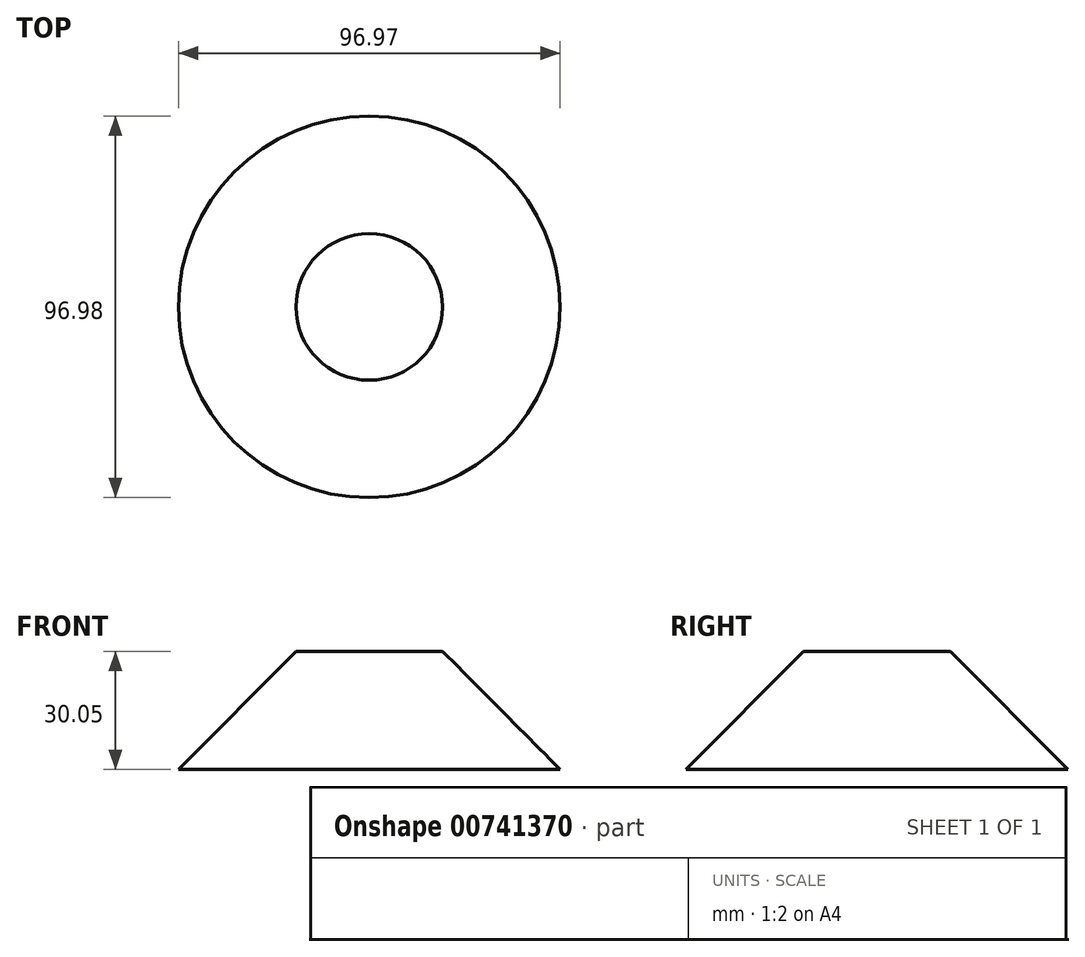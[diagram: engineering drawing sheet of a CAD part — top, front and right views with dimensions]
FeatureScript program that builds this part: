
annotation { "Feature Type Name" : "Feature", "Feature Type Description" : "" }
export const myFeature = defineFeature(function(context is Context, id is Id, definition is map)
    precondition{}
    {
        {
            var Q0;
            Q0=qCreatedBy(makeId("Front.planeOp"),FACE);
            var sketch = newSketch(context, id + "F0", { "sketchPlane" : qUnion([Q0])});
            skLineSegment(sketch, "E0", {"start": v(-63.33, 45.63) * mm, "end": v(-63.33, 15.58) * mm});
            skLineSegment(sketch, "E1", {"start": v(-63.33, 15.58) * mm, "end": v(-14.84, 15.58) * mm});
            skLineSegment(sketch, "E2", {"start": v(-63.33, 45.63) * mm, "end": v(-44.7, 45.63) * mm});
            skLineSegment(sketch, "E3", {"start": v(-44.7, 45.63) * mm, "end": v(-14.84, 15.58) * mm});
            skSolve(sketch);
        }
        {
            var Q0;
            Q0=makeQuery(id+"F0.imprint","IMPRINT",FACE,{"disambiguationData":[TD([[makeQuery(id+"F0.imprint","IMPRINT",EDGE,{"derivedFrom":sQuery(id+"F0.wireOp",EDGE,"E0")}),1.0]])]});
            var Q1;
            Q1=sQuery(id+"F0.wireOp",EDGE,"E0");
            revolve(context, id + "F1", {"surfaceOperationType" : NewSurfaceOperationType.NEW, "entities" : qUnion([Q0]), "axis" : qUnion([Q1]), "revolveType" : RevolveType.FULL});
        }
        {
            var Q0;
            Q0=qCreatedBy(makeId("Top.planeOp"),FACE);
            var sketch = newSketch(context, id + "F2", { "sketchPlane" : qUnion([Q0])});
            skLineSegment(sketch, "E4", {"start": v(-128.62, 27.68) * mm, "end": v(-14.1, 27.68) * mm});
            skSolve(sketch);
        }
        {
            var Q0;
            Q0=sQuery(id+"F2.wireOp",EDGE,"E4");
            extrude(context, id + "F3", {"bodyType" : ToolBodyType.SURFACE, "surfaceEntities" : qUnion([Q0]), "depth" : 57.66 * mm, "offsetDistance" : 25.4 * mm});
        }
    });
